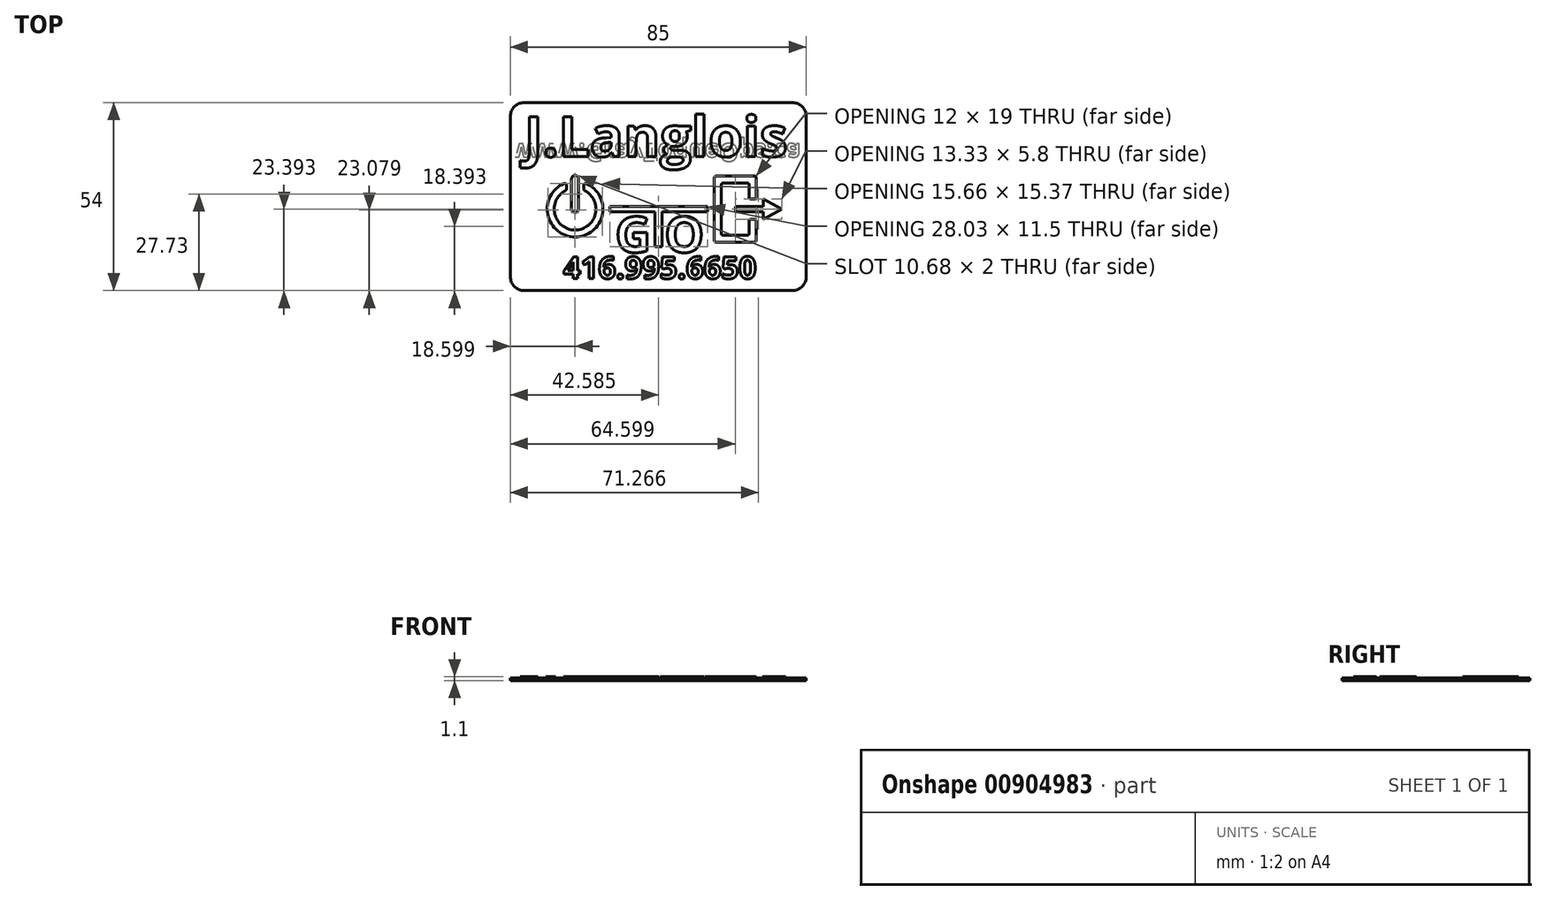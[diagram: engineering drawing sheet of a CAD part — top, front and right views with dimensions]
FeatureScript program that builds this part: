
annotation { "Feature Type Name" : "Feature", "Feature Type Description" : "" }
export const myFeature = defineFeature(function(context is Context, id is Id, definition is map)
    precondition{}
    {
        {
            var Q0;
            Q0=qCreatedBy(makeId("Top.planeOp"),FACE);
            var sketch = newSketch(context, id + "F0", { "sketchPlane" : qUnion([Q0])});
            skLineSegment(sketch, "E0.bottom", {"start": v(38.41, 27.17) * mm, "end": v(-38.59, 27.17) * mm});
            skLineSegment(sketch, "E0.top", {"start": v(38.41, -26.83) * mm, "end": v(-38.59, -26.83) * mm});
            skLineSegment(sketch, "E0.left", {"start": v(42.41, 23.17) * mm, "end": v(42.41, -22.83) * mm});
            skLineSegment(sketch, "E0.right", {"start": v(-42.59, 23.17) * mm, "end": v(-42.59, -22.83) * mm});
            skPoint(sketch, "E0.middle", {"position": v(-0.09, 0.17) * mm});
            skPoint(sketch, "E1.visualSharp", {"position": v(-42.59, 27.17) * mm});
            skArc(sketch, "E1.filletArc", {"start": v(-38.59, 27.17) * mm, "mid": v(-41.42, 26) * mm, "end": v(-42.59, 23.17) * mm});
            skPoint(sketch, "E2.visualSharp", {"position": v(42.41, 27.17) * mm});
            skArc(sketch, "E2.filletArc", {"start": v(42.41, 23.17) * mm, "mid": v(41.24, 26) * mm, "end": v(38.41, 27.17) * mm});
            skPoint(sketch, "E3.visualSharp", {"position": v(42.41, -26.83) * mm});
            skArc(sketch, "E3.filletArc", {"start": v(38.41, -26.83) * mm, "mid": v(41.24, -25.66) * mm, "end": v(42.41, -22.83) * mm});
            skPoint(sketch, "E4.visualSharp", {"position": v(-42.59, -26.83) * mm});
            skArc(sketch, "E4.filletArc", {"start": v(-42.59, -22.83) * mm, "mid": v(-41.42, -25.66) * mm, "end": v(-38.59, -26.83) * mm});
            skSolve(sketch);
        }
        {
            var Q0;
            Q0=makeQuery(id+"F0.imprint","IMPRINT",FACE,{"disambiguationData":[TD([[makeQuery(id+"F0.imprint","IMPRINT",EDGE,{"derivedFrom":sQuery(id+"F0.wireOp",EDGE,"E0.bottom")}),1.0]])]});
            extrude(context, id + "F1", {"entities" : qUnion([Q0]), "depth" : .8 * mm, "offsetDistance" : 25 * mm});
        }
        {
            var Q0;
            Q0=makeQuery(id+"F1.opExtrude","CAP_FACE",FACE,{"disambiguationData":[OSD([sQuery(id+"F0.wireOp",EDGE,"E0.bottom"),sQuery(id+"F0.wireOp",EDGE,"E0.top"),sQuery(id+"F0.wireOp",EDGE,"E0.left"),sQuery(id+"F0.wireOp",EDGE,"E0.right"),sQuery(id+"F0.wireOp",EDGE,"E1.filletArc"),sQuery(id+"F0.wireOp",EDGE,"E2.filletArc"),sQuery(id+"F0.wireOp",EDGE,"E3.filletArc"),sQuery(id+"F0.wireOp",EDGE,"E4.filletArc")])],"isStart":false});
            var sketch = newSketch(context, id + "F2", { "sketchPlane" : qUnion([Q0])});
            skArc(sketch, "E5", {"start": v(-26.76, 1.89) * mm, "mid": v(-24, -9.44) * mm, "end": v(-21.22, 1.89) * mm});
            skLineSegment(sketch, "E6.bottom", {"start": v(18.5, 4.06) * mm, "end": v(25.5, 4.06) * mm});
            skLineSegment(sketch, "E6.top", {"start": v(18.5, -10.94) * mm, "end": v(25.5, -10.94) * mm});
            skLineSegment(sketch, "E6.left", {"start": v(18, 3.56) * mm, "end": v(18, -10.44) * mm});
            skLineSegment(sketch, "E6.right", {"start": v(26, 3.56) * mm, "end": v(26, -0.04) * mm});
            skPoint(sketch, "E6.middle", {"position": v(22, -3.44) * mm});
            skLineSegment(sketch, "E7.0", {"start": v(16, 5.56) * mm, "end": v(16, -12.44) * mm});
            skLineSegment(sketch, "E7.1", {"start": v(16.5, 6.06) * mm, "end": v(27.5, 6.06) * mm});
            skLineSegment(sketch, "E7.2", {"start": v(28, 5.56) * mm, "end": v(28, -0.04) * mm});
            skLineSegment(sketch, "E7.3", {"start": v(16.5, -12.94) * mm, "end": v(27.5, -12.94) * mm});
            skArc(sketch, "E8.0.startCap", {"start": v(-23, -3.44) * mm, "mid": v(-24, -4.44) * mm, "end": v(-25, -3.44) * mm});
            skArc(sketch, "E8.0.endCap", {"start": v(-25, 5.24) * mm, "mid": v(-24, 6.24) * mm, "end": v(-23, 5.24) * mm});
            skLineSegment(sketch, "E8.0.left", {"start": v(-25, -3.44) * mm, "end": v(-25, 5.24) * mm});
            skLineSegment(sketch, "E8.0.right", {"start": v(-23, -3.44) * mm, "end": v(-23, 5.24) * mm});
            skArc(sketch, "E9.0", {"start": v(-27.2, 3.9) * mm, "mid": v(-24, -11.44) * mm, "end": v(-20.8, 3.9) * mm});
            skLineSegment(sketch, "E10", {"start": v(26.5, -0.54) * mm, "end": v(27.5, -0.54) * mm});
            skLineSegment(sketch, "E11.MirrorCS", {"start": v(26.5, -6.34) * mm, "end": v(27.5, -6.34) * mm});
            skLineSegment(sketch, "E12", {"start": v(-21.5, 2.33) * mm, "end": v(-21.5, 3.44) * mm});
            skLineSegment(sketch, "E13.MirrorCS", {"start": v(-26.5, 2.33) * mm, "end": v(-26.5, 3.44) * mm});
            skPoint(sketch, "E14.visualSharp", {"position": v(-21.5, 2.02) * mm});
            skArc(sketch, "E14.filletArc", {"start": v(-21.5, 2.33) * mm, "mid": v(-21.42, 2.07) * mm, "end": v(-21.22, 1.89) * mm});
            skPoint(sketch, "E15.visualSharp", {"position": v(-26.5, 2.02) * mm});
            skArc(sketch, "E15.filletArc", {"start": v(-26.76, 1.89) * mm, "mid": v(-26.56, 2.07) * mm, "end": v(-26.5, 2.33) * mm});
            skPoint(sketch, "E16.visualSharp", {"position": v(-26.5, 4.16) * mm});
            skArc(sketch, "E16.filletArc", {"start": v(-26.5, 3.44) * mm, "mid": v(-26.72, 3.85) * mm, "end": v(-27.2, 3.9) * mm});
            skPoint(sketch, "E17.visualSharp", {"position": v(-21.5, 4.16) * mm});
            skArc(sketch, "E17.filletArc", {"start": v(-20.8, 3.9) * mm, "mid": v(-21.27, 3.85) * mm, "end": v(-21.5, 3.44) * mm});
            skLineSegment(sketch, "E18.trimOffspring", {"start": v(26, -6.84) * mm, "end": v(26, -10.44) * mm});
            skLineSegment(sketch, "E19.trimOffspring", {"start": v(28, -6.84) * mm, "end": v(28, -12.44) * mm});
            skPoint(sketch, "E20.orphan", {"position": v(30.78, -3.44) * mm});
            skArc(sketch, "E21.0", {"start": v(-14.02, -4.19) * mm, "mid": v(-14, -3.44) * mm, "end": v(-14.02, -2.69) * mm});
            skLineSegment(sketch, "E22", {"start": v(37.15, -3.44) * mm, "end": v(-24, -3.44) * mm, "construction": true});
            skLineSegment(sketch, "E23", {"start": v(-14.02, -2.69) * mm, "end": v(14, -2.69) * mm});
            skLineSegment(sketch, "E24.MirrorCS", {"start": v(-14.02, -4.19) * mm, "end": v(-1, -4.19) * mm});
            skLineSegment(sketch, "E25", {"start": v(14, -2.69) * mm, "end": v(14, -4.19) * mm});
            skLineSegment(sketch, "E26.trimOffspring", {"start": v(22, -2.69) * mm, "end": v(30, -2.69) * mm});
            skLineSegment(sketch, "E27.trimOffspring", {"start": v(22, -4.19) * mm, "end": v(30, -4.19) * mm});
            skPoint(sketch, "E28.orphan", {"position": v(33.17, -2.69) * mm});
            skPoint(sketch, "E29.orphan", {"position": v(33.17, -4.19) * mm});
            skLineSegment(sketch, "E30", {"start": v(30.01, -6.34) * mm, "end": v(35.34, -3.44) * mm});
            skLineSegment(sketch, "E31", {"start": v(35.34, -3.44) * mm, "end": v(30.01, -0.54) * mm});
            skPoint(sketch, "E32.visualSharp", {"position": v(16, 6.06) * mm});
            skArc(sketch, "E32.filletArc", {"start": v(16.5, 6.06) * mm, "mid": v(16.16, 5.92) * mm, "end": v(16, 5.56) * mm});
            skPoint(sketch, "E33.visualSharp", {"position": v(28, 6.06) * mm});
            skArc(sketch, "E33.filletArc", {"start": v(28, 5.56) * mm, "mid": v(27.86, 5.92) * mm, "end": v(27.5, 6.06) * mm});
            skPoint(sketch, "E34.visualSharp", {"position": v(28, -0.54) * mm});
            skArc(sketch, "E34.filletArc", {"start": v(27.5, -0.54) * mm, "mid": v(27.86, -0.4) * mm, "end": v(28, -0.04) * mm});
            skPoint(sketch, "E35.visualSharp", {"position": v(26, -0.54) * mm});
            skArc(sketch, "E35.filletArc", {"start": v(26, -0.04) * mm, "mid": v(26.16, -0.4) * mm, "end": v(26.5, -0.54) * mm});
            skPoint(sketch, "E36.visualSharp", {"position": v(26, -6.34) * mm});
            skArc(sketch, "E36.filletArc", {"start": v(26.5, -6.34) * mm, "mid": v(26.16, -6.48) * mm, "end": v(26, -6.84) * mm});
            skPoint(sketch, "E37.visualSharp", {"position": v(28, -6.34) * mm});
            skArc(sketch, "E37.filletArc", {"start": v(28, -6.84) * mm, "mid": v(27.86, -6.48) * mm, "end": v(27.5, -6.34) * mm});
            skPoint(sketch, "E38.visualSharp", {"position": v(28, -12.94) * mm});
            skArc(sketch, "E38.filletArc", {"start": v(27.5, -12.94) * mm, "mid": v(27.86, -12.8) * mm, "end": v(28, -12.44) * mm});
            skPoint(sketch, "E39.visualSharp", {"position": v(16, -12.94) * mm});
            skArc(sketch, "E39.filletArc", {"start": v(16, -12.44) * mm, "mid": v(16.16, -12.8) * mm, "end": v(16.5, -12.94) * mm});
            skPoint(sketch, "E40.visualSharp", {"position": v(18, -10.94) * mm});
            skArc(sketch, "E40.filletArc", {"start": v(18, -10.44) * mm, "mid": v(18.16, -10.8) * mm, "end": v(18.5, -10.94) * mm});
            skPoint(sketch, "E41.visualSharp", {"position": v(26, -10.94) * mm});
            skArc(sketch, "E41.filletArc", {"start": v(25.5, -10.94) * mm, "mid": v(25.86, -10.8) * mm, "end": v(26, -10.44) * mm});
            skPoint(sketch, "E42.visualSharp", {"position": v(26, 4.06) * mm});
            skArc(sketch, "E42.filletArc", {"start": v(26, 3.56) * mm, "mid": v(25.86, 3.92) * mm, "end": v(25.5, 4.06) * mm});
            skPoint(sketch, "E43.visualSharp", {"position": v(18, 4.06) * mm});
            skArc(sketch, "E43.filletArc", {"start": v(18.5, 4.06) * mm, "mid": v(18.16, 3.92) * mm, "end": v(18, 3.56) * mm});
            skLineSegment(sketch, "E44", {"start": v(30, -4.19) * mm, "end": v(30.01, -6.34) * mm});
            skLineSegment(sketch, "E45", {"start": v(30, -2.69) * mm, "end": v(30.01, -0.54) * mm});
            skLineSegment(sketch, "E46", {"start": v(0, 6.56) * mm, "end": v(0, -14.35) * mm, "construction": true});
            skLineSegment(sketch, "E47", {"start": v(-1, -4.19) * mm, "end": v(-1, -14.19) * mm});
            skPoint(sketch, "E48.orphan", {"position": v(-1, 2.46) * mm});
            skPoint(sketch, "E49.orphan", {"position": v(1, 2.46) * mm});
            skLineSegment(sketch, "E50.trimOffspring", {"start": v(1, -4.19) * mm, "end": v(1, -14.19) * mm});
            skLineSegment(sketch, "E51.trimOffspring", {"start": v(1, -4.19) * mm, "end": v(14, -4.19) * mm});
            skLineSegment(sketch, "E52", {"start": v(-1, -14.19) * mm, "end": v(1, -14.19) * mm});
            skLineSegment(sketch, "E53", {"start": v(22, -2.69) * mm, "end": v(22, -4.19) * mm});
            skSolve(sketch);
        }
        {
            var Q0;
            Q0 = qSketchRegion(id + "F2", true);
            extrude(context, id + "F3", {"entities" : qUnion([Q0]), "operationType" : NewBodyOperationType.REMOVE, "endBound" : BoundingType.THROUGH_ALL, "oppositeDirection" : true, "depth" : 25 * mm, "offsetDistance" : 25 * mm});
        }
        {
            var Q0;
            Q0=makeQuery(id+"F1.opExtrude","CAP_FACE",FACE,{"disambiguationData":[OSD([sQuery(id+"F0.wireOp",EDGE,"E0.bottom"),sQuery(id+"F0.wireOp",EDGE,"E0.top"),sQuery(id+"F0.wireOp",EDGE,"E0.left"),sQuery(id+"F0.wireOp",EDGE,"E0.right"),sQuery(id+"F0.wireOp",EDGE,"E1.filletArc"),sQuery(id+"F0.wireOp",EDGE,"E2.filletArc"),sQuery(id+"F0.wireOp",EDGE,"E3.filletArc"),sQuery(id+"F0.wireOp",EDGE,"E4.filletArc")])],"isStart":true});
            var sketch = newSketch(context, id + "F4", { "sketchPlane" : qUnion([Q0])});
            skText(sketch, "E54", { "text": "www.GrayToqueOps.ca", "fontName": "OpenSans-Bold.ttf"});
            const initialGuessF4  = {"E54": [-0.0412, -0.0154, 1, 0, 0.00509]};
            skSetInitialGuess(sketch, initialGuessF4);
            skSolve(sketch);
        }
        {
            var Q0;
            Q0 = qSketchRegion(id + "F4", true);
            extrude(context, id + "F5", {"entities" : qUnion([Q0]), "operationType" : NewBodyOperationType.REMOVE, "oppositeDirection" : true, "depth" : .3 * mm, "offsetDistance" : 25 * mm});
        }
        {
            var Q0;
            Q0=makeQuery(id+"F1.opExtrude","CAP_FACE",FACE,{"disambiguationData":[OSD([sQuery(id+"F0.wireOp",EDGE,"E0.bottom"),sQuery(id+"F0.wireOp",EDGE,"E0.top"),sQuery(id+"F0.wireOp",EDGE,"E0.left"),sQuery(id+"F0.wireOp",EDGE,"E0.right"),sQuery(id+"F0.wireOp",EDGE,"E1.filletArc"),sQuery(id+"F0.wireOp",EDGE,"E2.filletArc"),sQuery(id+"F0.wireOp",EDGE,"E3.filletArc"),sQuery(id+"F0.wireOp",EDGE,"E4.filletArc")])],"isStart":false});
            var sketch = newSketch(context, id + "F6", { "sketchPlane" : qUnion([Q0])});
            skText(sketch, "E55", { "text": "J.Langlois", "fontName": "OpenSans-Bold.ttf"});
            skText(sketch, "E56", { "text": "416.995.6650", "fontName": "OpenSans-Bold.ttf"});
            skText(sketch, "E57", { "text": "G", "fontName": "OpenSans-Bold.ttf"});
            skText(sketch, "E58", { "text": "O", "fontName": "OpenSans-Bold.ttf"});
            const initialGuessF6  = {"E55": [-0.03859, 0.01167, 1, 0, 0.0115], "E56": [-0.02739, -0.02342, 1, 0, 0.00636], "E57": [-0.01249, -0.01586, 1, 0, 0.0103], "E58": [0.00168, -0.01586, 1, 0, 0.0103]};
            skSetInitialGuess(sketch, initialGuessF6);
            skSolve(sketch);
        }
        {
            var Q0;
            Q0 = qSketchRegion(id + "F6", true);
            extrude(context, id + "F7", {"entities" : qUnion([Q0]), "operationType" : NewBodyOperationType.ADD, "depth" : .3 * mm, "offsetDistance" : 25 * mm});
        }
    });
